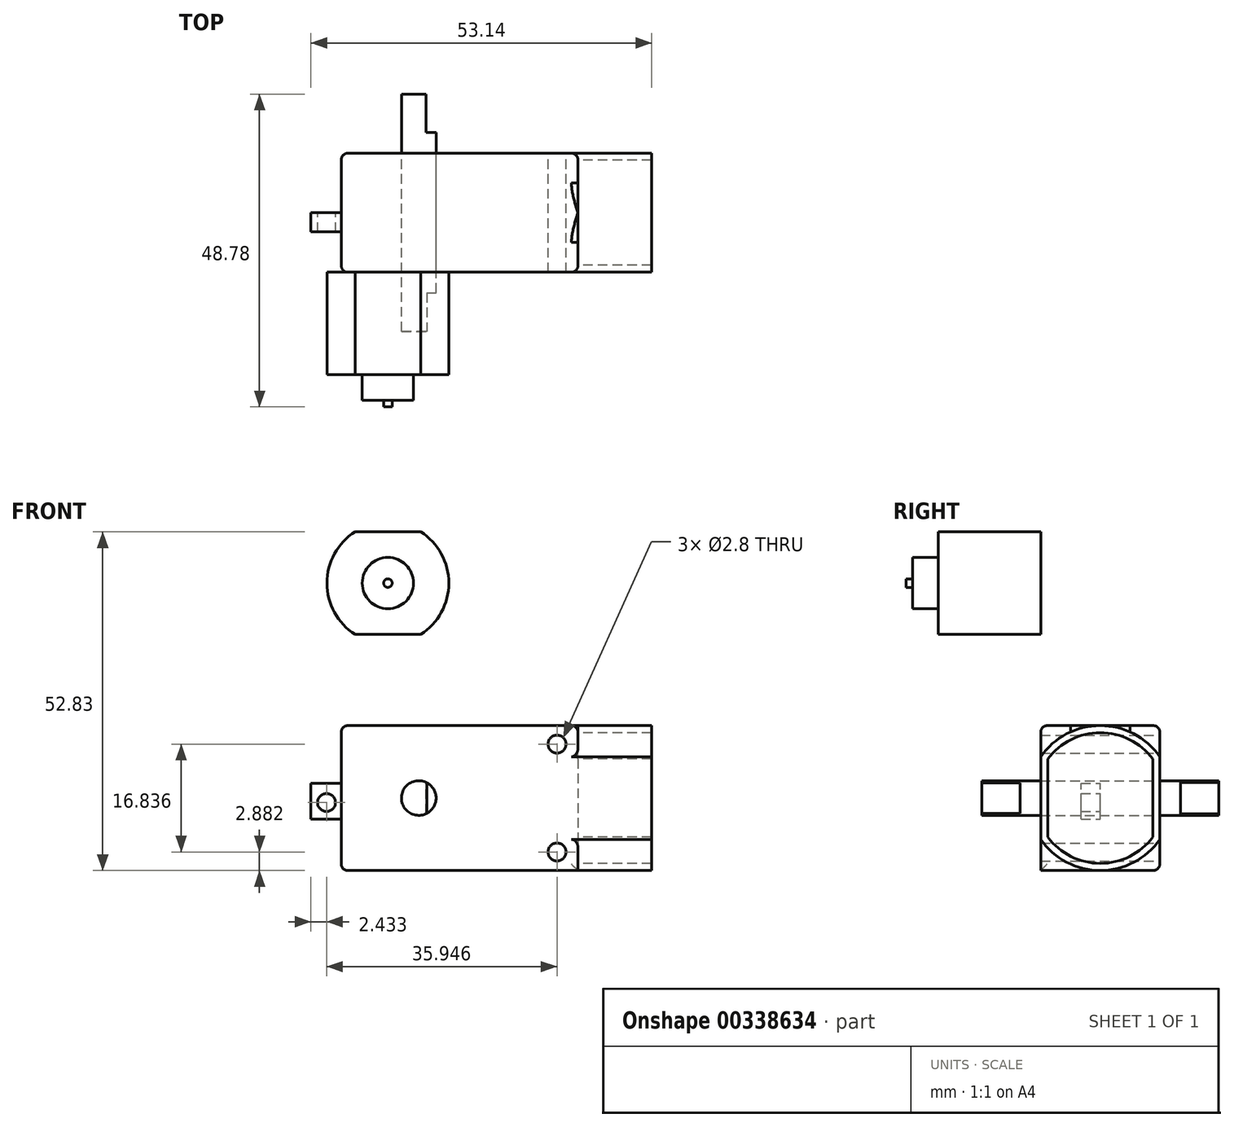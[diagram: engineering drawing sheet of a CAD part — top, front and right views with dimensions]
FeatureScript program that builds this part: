
annotation { "Feature Type Name" : "Feature", "Feature Type Description" : "" }
export const myFeature = defineFeature(function(context is Context, id is Id, definition is map)
    precondition{}
    {
        {
            var Q0;
            Q0=qCreatedBy(makeId("Front.planeOp"),FACE);
            var sketch = newSketch(context, id + "F0", { "sketchPlane" : qUnion([Q0])});
            skLineSegment(sketch, "E0.bottom", {"start": v(-10.04, -11.3) * mm, "end": v(-46.94, -11.3) * mm});
            skLineSegment(sketch, "E0.top", {"start": v(-10.04, 11.3) * mm, "end": v(-46.94, 11.3) * mm});
            skLineSegment(sketch, "E0.right", {"start": v(-46.94, -11.3) * mm, "end": v(-46.94, 11.3) * mm});
            skPoint(sketch, "E0.middle", {"position": v(-20.83, 0) * mm});
            skPoint(sketch, "E1.middle", {"position": v(8.58, 0) * mm});
            skCircle(sketch, "E2", {"center": v(-34.86, 0) * mm, "radius": 2.7 * mm});
            skLineSegment(sketch, "E3.bottom", {"start": v(-46.94, -3.26) * mm, "end": v(-51.68, -3.26) * mm});
            skLineSegment(sketch, "E3.top", {"start": v(-46.94, 2.31) * mm, "end": v(-51.68, 2.31) * mm});
            skLineSegment(sketch, "E3.left", {"start": v(-46.94, -3.26) * mm, "end": v(-46.94, 2.31) * mm});
            skLineSegment(sketch, "E3.right", {"start": v(-51.68, -3.26) * mm, "end": v(-51.68, 2.31) * mm});
            skCircle(sketch, "E4", {"center": v(-49.25, -0.7) * mm, "radius": 1.4 * mm});
            skLineSegment(sketch, "E5", {"start": v(-10.04, 11.3) * mm, "end": v(-10.04, -11.3) * mm});
            skPoint(sketch, "E6.orphan", {"position": v(5.29, 11.3) * mm});
            skPoint(sketch, "E7.orphan", {"position": v(5.29, -11.3) * mm});
            skCircle(sketch, "E8", {"center": v(-13.3, 8.42) * mm, "radius": 1.4 * mm});
            skCircle(sketch, "E9.MirrorC", {"center": v(-13.3, -8.42) * mm, "radius": 1.4 * mm});
            skSolve(sketch);
        }
        {
            var Q0;
            {var subQ9=sQuery(id+"F0.wireOp",EDGE,"E0.bottom");Q0=makeQuery(id+"F0.imprint","IMPRINT",FACE,{"disambiguationData":[TD([[makeQuery(id+"F0.imprint","IMPRINT",EDGE,{"derivedFrom":subQ9}),-1.0]])]});}
            var Q1;
            {var subQ5=sQuery(id+"F0.wireOp",EDGE,"E1.left");Q1=makeQuery(id+"F0.imprint","IMPRINT",FACE,{"disambiguationData":[TD([[makeQuery(id+"F0.imprint","IMPRINT",EDGE,{"derivedFrom":subQ5}),1.0]])]});}
            var Q2;
            {var subQ5=sQuery(id+"F0.wireOp",EDGE,"E1.right");Q2=makeQuery(id+"F0.imprint","IMPRINT",FACE,{"disambiguationData":[TD([[makeQuery(id+"F0.imprint","IMPRINT",EDGE,{"derivedFrom":subQ5}),-1.0]])]});}
            extrude(context, id + "F1", {"entities" : qUnion([Q0, Q1, Q2]), "depth" : 18.56 * mm, "offsetDistance" : 25 * mm, "symmetric" : true});
        }
        {
            var Q0;
            Q0=makeQuery(id+"F1.opExtrude","SWEPT_FACE",FACE,{"disambiguationData":[OSD([sQuery(id+"F0.wireOp",EDGE,"E5")])]});
            var sketch = newSketch(context, id + "F2", { "sketchPlane" : qUnion([Q0])});
            skArc(sketch, "E10", {"start": v(-9.28, -6.45) * mm, "mid": v(0, -11.3) * mm, "end": v(9.28, -6.45) * mm});
            skLineSegment(sketch, "E11.0", {"start": v(-9.28, 6.45) * mm, "end": v(-9.28, -6.45) * mm});
            skLineSegment(sketch, "E11.1", {"start": v(9.28, 6.45) * mm, "end": v(9.28, -6.45) * mm});
            skArc(sketch, "E12.trimOffspring", {"start": v(9.28, 6.45) * mm, "mid": v(0, 11.3) * mm, "end": v(-9.28, 6.45) * mm});
            skPoint(sketch, "E13.orphan", {"position": v(-9.28, 11.3) * mm});
            skPoint(sketch, "E14.orphan", {"position": v(-9.28, -11.3) * mm});
            skPoint(sketch, "E15.orphan", {"position": v(9.28, -11.3) * mm});
            skPoint(sketch, "E16.orphan", {"position": v(9.28, 11.3) * mm});
            skArc(sketch, "E17.0", {"start": v(8.18, 6.1) * mm, "mid": v(0, 10.2) * mm, "end": v(-8.18, 6.1) * mm});
            skLineSegment(sketch, "E17.1", {"start": v(8.18, 6.1) * mm, "end": v(8.18, -6.1) * mm});
            skArc(sketch, "E17.2", {"start": v(-8.18, -6.1) * mm, "mid": v(0, -10.2) * mm, "end": v(8.18, -6.1) * mm});
            skLineSegment(sketch, "E17.3", {"start": v(-8.18, 6.1) * mm, "end": v(-8.18, -6.1) * mm});
            skSolve(sketch);
        }
        {
            var Q0;
            {var subQ1=sQuery(id+"F2.wireOp",EDGE,"E11.0");Q0=makeQuery(id+"F2.imprint","IMPRINT",FACE,{"disambiguationData":[TD([[makeQuery(id+"F2.imprint","IMPRINT",EDGE,{"derivedFrom":subQ1}),1.0]])]});}
            extrude(context, id + "F3", {"entities" : qUnion([Q0]), "operationType" : NewBodyOperationType.ADD, "depth" : 11.5 * mm});
        }
        {
            var Q0;
            Q0=makeQuery(id+"F0.imprint","IMPRINT",FACE,{"disambiguationData":[TD([[makeQuery(id+"F0.imprint","IMPRINT",EDGE,{"derivedFrom":sQuery(id+"F0.wireOp",EDGE,"E3.bottom")}),-1.0]])]});
            extrude(context, id + "F4", {"entities" : qUnion([Q0]), "operationType" : NewBodyOperationType.ADD, "depth" : 3 * mm});
        }
        {
            var Q0;
            Q0=makeQuery(id+"F0.imprint","IMPRINT",FACE,{"disambiguationData":[TD([[makeQuery(id+"F0.imprint","IMPRINT",EDGE,{"derivedFrom":sQuery(id+"F0.wireOp",EDGE,"E2")}),1.0]])]});
            extrude(context, id + "F5", {"entities" : qUnion([Q0]), "depth" : 37 * mm, "symmetric" : true});
        }
        {
            var Q0;
            Q0=makeQuery(id+"F5.opExtrude","CAP_FACE",FACE,{"disambiguationData":[OSD([sQuery(id+"F0.wireOp",EDGE,"E2")])],"isStart":false});
            var sketch = newSketch(context, id + "F6", { "sketchPlane" : qUnion([Q0])});
            skCircle(sketch, "E18.0.0", {"center": v(-34.86, 0) * mm, "radius": 2.7 * mm});
            skLineSegment(sketch, "E19", {"start": v(-33.6, 2.39) * mm, "end": v(-33.6, -2.39) * mm});
            skSolve(sketch);
        }
        {
            var Q0;
            {var subQ0=sQuery(id+"F6.wireOp",EDGE,"E19");Q0=makeQuery(id+"F6.imprint","IMPRINT",FACE,{"disambiguationData":[TD([[makeQuery(id+"F6.imprint","IMPRINT",EDGE,{"derivedFrom":subQ0}),1.0]])]});}
            extrude(context, id + "F7", {"entities" : qUnion([Q0]), "operationType" : NewBodyOperationType.REMOVE, "oppositeDirection" : true, "depth" : 6 * mm});
        }
        {
            var Q0;
            Q0=makeQuery(id+"F5.opExtrude","CAP_FACE",FACE,{"disambiguationData":[OSD([sQuery(id+"F0.wireOp",EDGE,"E2")])],"isStart":true});
            var sketch = newSketch(context, id + "F8", { "sketchPlane" : qUnion([Q0])});
            skLineSegment(sketch, "E20", {"start": v(33.7, -2.44) * mm, "end": v(33.7, 2.44) * mm});
            skSolve(sketch);
        }
        {
            var Q0;
            {var subQ0=sQuery(id+"F8.wireOp",EDGE,"E20");Q0=makeQuery(id+"F8.imprint","IMPRINT",FACE,{"disambiguationData":[TD([[makeQuery(id+"F8.imprint","IMPRINT",EDGE,{"derivedFrom":subQ0}),1.0]])]});}
            extrude(context, id + "F9", {"entities" : qUnion([Q0]), "operationType" : NewBodyOperationType.REMOVE, "oppositeDirection" : true, "depth" : 6 * mm});
        }
        {
            var Q0;
            Q0=makeQuery(id+"F3.boolean.opBoolean","MERGE",FACE,{"derivedFrom":[makeQuery(id+"F1.opExtrude","CAP_FACE",FACE,{"disambiguationData":[OSD([sQuery(id+"F0.wireOp",EDGE,"E0.bottom"),sQuery(id+"F0.wireOp",EDGE,"E0.top"),sQuery(id+"F0.wireOp",EDGE,"E0.right"),sQuery(id+"F0.wireOp",EDGE,"E2"),sQuery(id+"F0.wireOp",EDGE,"E3.left"),sQuery(id+"F0.wireOp",EDGE,"E5"),sQuery(id+"F0.wireOp",EDGE,"E8"),sQuery(id+"F0.wireOp",EDGE,"E9.MirrorC")])],"isStart":false}),makeQuery(id+"F3.opExtrude","SWEPT_FACE",FACE,{"disambiguationData":[OSD([sQuery(id+"F2.wireOp",EDGE,"E11.0")])]})]});
            var sketch = newSketch(context, id + "F10", { "sketchPlane" : qUnion([Q0])});
            skArc(sketch, "E21", {"start": v(-44.8, 41.53) * mm, "mid": v(-49.18, 33.53) * mm, "end": v(-44.8, 25.53) * mm});
            skLineSegment(sketch, "E22.bottom", {"start": v(-44.8, 41.53) * mm, "end": v(-34.56, 41.53) * mm});
            skLineSegment(sketch, "E22.top", {"start": v(-44.8, 25.53) * mm, "end": v(-34.56, 25.53) * mm});
            skArc(sketch, "E23.trimOffspring", {"start": v(-34.56, 25.53) * mm, "mid": v(-30.18, 33.53) * mm, "end": v(-34.56, 41.53) * mm});
            skSolve(sketch);
        }
        {
            var Q0;
            Q0 = qSketchRegion(id + "F10", true);
            extrude(context, id + "F11", {"entities" : qUnion([Q0]), "depth" : 16 * mm});
        }
        {
            var Q0;
            Q0=makeQuery(id+"F11.opExtrude","CAP_FACE",FACE,{"disambiguationData":[OSD([sQuery(id+"F10.wireOp",EDGE,"E21"),sQuery(id+"F10.wireOp",EDGE,"E22.bottom"),sQuery(id+"F10.wireOp",EDGE,"E22.top"),sQuery(id+"F10.wireOp",EDGE,"E23.trimOffspring")])],"isStart":false});
            var sketch = newSketch(context, id + "F12", { "sketchPlane" : qUnion([Q0])});
            skCircle(sketch, "E24", {"center": v(-39.68, 33.53) * mm, "radius": 4 * mm});
            skCircle(sketch, "E25", {"center": v(-39.68, 33.53) * mm, "radius": 0.67 * mm});
            skSolve(sketch);
        }
        {
            var Q0;
            Q0=makeQuery(id+"F12.imprint","IMPRINT",FACE,{"disambiguationData":[TD([[makeQuery(id+"F12.imprint","IMPRINT",EDGE,{"derivedFrom":sQuery(id+"F12.wireOp",EDGE,"E24")}),1.0]])]});
            extrude(context, id + "F13", {"entities" : qUnion([Q0]), "operationType" : NewBodyOperationType.ADD, "depth" : 4 * mm});
        }
        {
            var Q0;
            Q0=makeQuery(id+"F13.boolean.opBoolean","SPLIT",FACE,{"disambiguationData":[TD([makeQuery(id+"F13.opExtrude","SWEPT_FACE",FACE,{"disambiguationData":[OSD([sQuery(id+"F12.wireOp",EDGE,"E25")])]})])],"derivedFrom":makeQuery(id+"F11.opExtrude","CAP_FACE",FACE,{"disambiguationData":[OSD([sQuery(id+"F10.wireOp",EDGE,"E21"),sQuery(id+"F10.wireOp",EDGE,"E22.bottom"),sQuery(id+"F10.wireOp",EDGE,"E22.top"),sQuery(id+"F10.wireOp",EDGE,"E23.trimOffspring")])],"isStart":false})});
            extrude(context, id + "F14", {"entities" : qUnion([Q0]), "operationType" : NewBodyOperationType.ADD, "depth" : 5 * mm});
        }
        {
            var Q0;
            Q0=makeQuery(id+"F1.opExtrude","CAP_EDGE",EDGE,{"disambiguationData":[OSD([sQuery(id+"F0.wireOp",EDGE,"E0.top")])],"isStart":false});
            var Q1;
            {var subQ0=sQuery(id+"F0.wireOp",EDGE,"E5");var subQ1=sQuery(id+"F0.wireOp",EDGE,"E0.top");Q1=makeQuery(id+"F3.boolean.opBoolean","SPLIT",EDGE,{"disambiguationData":[TD([makeQuery(id+"F3.opExtrude","SWEPT_FACE",FACE,{"disambiguationData":[OSD([sQuery(id+"F2.wireOp",EDGE,"E11.0")])]})])],"derivedFrom":makeQuery(id+"F1.opExtrude","SWEPT_EDGE",EDGE,{"disambiguationData":[OSD([subQ1,subQ0])]})});}
            var Q2;
            {var subQ0=sQuery(id+"F0.wireOp",EDGE,"E0.top");var subQ1=sQuery(id+"F0.wireOp",EDGE,"E5");Q2=makeQuery(id+"F3.boolean.opBoolean","SPLIT",EDGE,{"disambiguationData":[TD([makeQuery(id+"F3.opExtrude","SWEPT_FACE",FACE,{"disambiguationData":[OSD([sQuery(id+"F2.wireOp",EDGE,"E11.1")])]})])],"derivedFrom":makeQuery(id+"F1.opExtrude","SWEPT_EDGE",EDGE,{"disambiguationData":[OSD([subQ0,subQ1])]})});}
            var Q3;
            Q3=makeQuery(id+"F1.opExtrude","CAP_EDGE",EDGE,{"disambiguationData":[OSD([sQuery(id+"F0.wireOp",EDGE,"E0.top")])],"isStart":true});
            var Q4;
            Q4=makeQuery(id+"F1.opExtrude","SWEPT_EDGE",EDGE,{"disambiguationData":[OSD([sQuery(id+"F0.wireOp",EDGE,"E0.top"),sQuery(id+"F0.wireOp",EDGE,"E0.right")])]});
            var Q5;
            Q5=makeQuery(id+"F1.opExtrude","CAP_EDGE",EDGE,{"disambiguationData":[OSD([sQuery(id+"F0.wireOp",EDGE,"E0.right"),sQuery(id+"F0.wireOp",EDGE,"E3.left")])],"isStart":true});
            var Q6;
            Q6=makeQuery(id+"F1.opExtrude","CAP_EDGE",EDGE,{"disambiguationData":[OSD([sQuery(id+"F0.wireOp",EDGE,"E0.bottom")])],"isStart":true});
            var Q7;
            {var subQ0=sQuery(id+"F0.wireOp",EDGE,"E5");var subQ1=sQuery(id+"F0.wireOp",EDGE,"E0.bottom");Q7=makeQuery(id+"F3.boolean.opBoolean","SPLIT",EDGE,{"disambiguationData":[TD([makeQuery(id+"F1.opExtrude","SWEPT_FACE",FACE,{"disambiguationData":[OSD([subQ1])]})])],"derivedFrom":makeQuery(id+"F1.opExtrude","CAP_EDGE",EDGE,{"disambiguationData":[OSD([subQ0])],"isStart":true})});}
            var Q8;
            {var subQ0=sQuery(id+"F0.wireOp",EDGE,"E0.top");var subQ1=sQuery(id+"F0.wireOp",EDGE,"E5");Q8=makeQuery(id+"F3.boolean.opBoolean","SPLIT",EDGE,{"disambiguationData":[TD([makeQuery(id+"F1.opExtrude","SWEPT_FACE",FACE,{"disambiguationData":[OSD([subQ0])]})])],"derivedFrom":makeQuery(id+"F1.opExtrude","CAP_EDGE",EDGE,{"disambiguationData":[OSD([subQ1])],"isStart":true})});}
            var Q9;
            Q9=makeQuery(id+"F1.opExtrude","CAP_EDGE",EDGE,{"disambiguationData":[OSD([sQuery(id+"F0.wireOp",EDGE,"E0.right"),sQuery(id+"F0.wireOp",EDGE,"E3.left")])],"isStart":false});
            var Q10;
            Q10=makeQuery(id+"F1.opExtrude","SWEPT_EDGE",EDGE,{"disambiguationData":[OSD([sQuery(id+"F0.wireOp",EDGE,"E0.bottom"),sQuery(id+"F0.wireOp",EDGE,"E0.right")])]});
            fillet(context, id + "F15", {"entities" : qUnion([Q0, Q1, Q2, Q3, Q4, Q5, Q6, Q7, Q8, Q9, Q10]), "radius" : 1 * mm, "tangentPropagation" : true, "allowEdgeOverflow" : false});
        }
        {
            var Q0;
            {var subQ0=sQuery(id+"F0.wireOp",EDGE,"E5");var subQ1=sQuery(id+"F0.wireOp",EDGE,"E0.bottom");Q0=makeQuery(id+"F3.boolean.opBoolean","SPLIT",EDGE,{"disambiguationData":[TD([makeQuery(id+"F1.opExtrude","SWEPT_FACE",FACE,{"disambiguationData":[OSD([subQ1])]})])],"derivedFrom":makeQuery(id+"F1.opExtrude","CAP_EDGE",EDGE,{"disambiguationData":[OSD([subQ0])],"isStart":false})});}
            var Q1;
            {var subQ0=sQuery(id+"F0.wireOp",EDGE,"E5");var subQ1=sQuery(id+"F0.wireOp",EDGE,"E0.top");Q1=makeQuery(id+"F3.boolean.opBoolean","SPLIT",EDGE,{"disambiguationData":[TD([makeQuery(id+"F1.opExtrude","SWEPT_FACE",FACE,{"disambiguationData":[OSD([subQ1])]})])],"derivedFrom":makeQuery(id+"F1.opExtrude","CAP_EDGE",EDGE,{"disambiguationData":[OSD([subQ0])],"isStart":false})});}
            fillet(context, id + "F16", {"entities" : qUnion([Q0, Q1]), "radius" : 1 * mm, "tangentPropagation" : true, "allowEdgeOverflow" : false});
        }
    });
